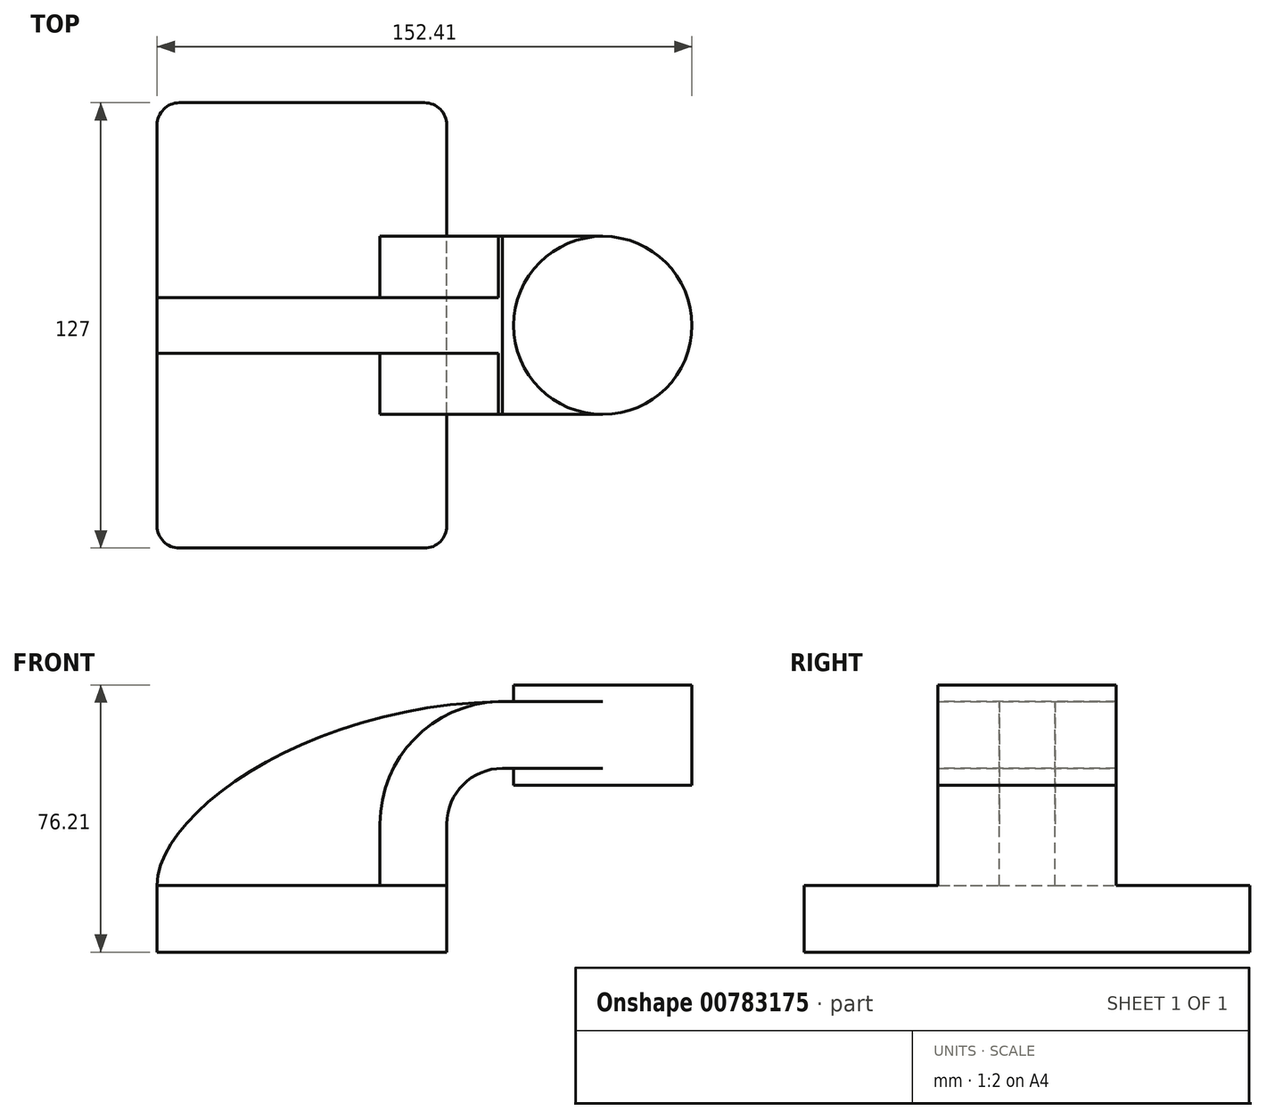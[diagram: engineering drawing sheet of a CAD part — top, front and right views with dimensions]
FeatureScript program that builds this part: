
annotation { "Feature Type Name" : "Feature", "Feature Type Description" : "" }
export const myFeature = defineFeature(function(context is Context, id is Id, definition is map)
    precondition{}
    {
        {
            var Q0;
            Q0=qCreatedBy(makeId("Front.planeOp"),FACE);
            var sketch = newSketch(context, id + "F0", { "sketchPlane" : qUnion([Q0])});
            skLineSegment(sketch, "E0.bottom", {"start": v(41.28, -9.52) * mm, "end": v(-41.28, -9.53) * mm});
            skLineSegment(sketch, "E0.top", {"start": v(41.28, 9.53) * mm, "end": v(-41.28, 9.53) * mm});
            skLineSegment(sketch, "E0.left", {"start": v(41.28, -9.52) * mm, "end": v(41.28, 9.53) * mm});
            skLineSegment(sketch, "E0.right", {"start": v(-41.28, -9.52) * mm, "end": v(-41.28, 9.53) * mm});
            skPoint(sketch, "E0.middle", {"position": v(0, 0) * mm});
            skLineSegment(sketch, "E1.bottom", {"start": v(60.32, 66.68) * mm, "end": v(111.13, 66.68) * mm});
            skLineSegment(sketch, "E1.top", {"start": v(60.32, 38.1) * mm, "end": v(111.13, 38.1) * mm});
            skLineSegment(sketch, "E1.left", {"start": v(60.32, 66.68) * mm, "end": v(60.32, 38.1) * mm});
            skLineSegment(sketch, "E1.right", {"start": v(111.13, 66.68) * mm, "end": v(111.13, 38.1) * mm});
            skPoint(sketch, "E1.middle", {"position": v(85.72, 52.39) * mm});
            skLineSegment(sketch, "E2", {"start": v(41.28, 9.53) * mm, "end": v(41.28, 27) * mm});
            skArc(sketch, "E3", {"start": v(41.27, 27) * mm, "mid": v(45.92, 38.23) * mm, "end": v(57.15, 42.88) * mm});
            skLineSegment(sketch, "E4", {"start": v(57.15, 42.88) * mm, "end": v(85.72, 42.88) * mm});
            skLineSegment(sketch, "E5.0", {"start": v(57.15, 61.93) * mm, "end": v(85.72, 61.93) * mm});
            skArc(sketch, "E5.1", {"start": v(22.23, 27) * mm, "mid": v(32.45, 51.7) * mm, "end": v(57.15, 61.93) * mm});
            skLineSegment(sketch, "E5.2", {"start": v(22.22, 9.53) * mm, "end": v(22.22, 27) * mm});
            skLineSegment(sketch, "E6", {"start": v(85.72, 66.68) * mm, "end": v(85.72, 38.1) * mm});
            skFitSpline(sketch, "E7", {"points": [v(-41.28, 9.52) * mm, v(57.15, 61.93) * mm], "startDerivative": vector(0.87, 64.38) * mm, "endDerivative": vector(161.64, 2.04) * mm});
            skSolve(sketch);
        }
        {
            var Q0;
            Q0=makeQuery(id+"F0.imprint","IMPRINT",FACE,{"disambiguationData":[TD([[makeQuery(id+"F0.imprint","IMPRINT",EDGE,{"derivedFrom":sQuery(id+"F0.wireOp",EDGE,"E0.bottom")}),-1.0]])]});
            extrude(context, id + "F1", {"entities" : qUnion([Q0]), "endBound" : BoundingType.SYMMETRIC, "depth" : 127 * mm, "offsetDistance" : 25.4 * mm});
        }
        {
            var Q0;
            {var subQ1=sQuery(id+"F0.wireOp",EDGE,"E2");Q0=makeQuery(id+"F0.imprint","IMPRINT",FACE,{"disambiguationData":[TD([[makeQuery(id+"F0.imprint","IMPRINT",EDGE,{"derivedFrom":subQ1}),1.0]])]});}
            var Q1;
            {var subQ0=sQuery(id+"F0.wireOp",EDGE,"E5.0");var subQ1=sQuery(id+"F0.wireOp",EDGE,"E1.left");var subQ2=makeQuery(id+"F0.imprint","INTERSECT",VERTEX,{"derivedFrom":[subQ1,subQ0]});Q1=makeQuery(id+"F0.imprint","IMPRINT",FACE,{"disambiguationData":[TD([[makeQuery(id+"F0.imprint","IMPRINT",EDGE,{"disambiguationData":[TD([[subQ2,-1.0]])],"derivedFrom":subQ1}),1.0]])]});}
            extrude(context, id + "F2", {"entities" : qUnion([Q0, Q1]), "operationType" : NewBodyOperationType.ADD, "endBound" : BoundingType.SYMMETRIC, "depth" : 50.8 * mm, "offsetDistance" : 25.4 * mm});
        }
        {
            var Q0;
            {var subQ3=sQuery(id+"F0.wireOp",EDGE,"E5.2");Q0=makeQuery(id+"F0.imprint","IMPRINT",FACE,{"disambiguationData":[TD([[makeQuery(id+"F0.imprint","IMPRINT",EDGE,{"derivedFrom":subQ3}),1.0]])]});}
            extrude(context, id + "F3", {"entities" : qUnion([Q0]), "operationType" : NewBodyOperationType.ADD, "endBound" : BoundingType.SYMMETRIC, "depth" : 15.88 * mm, "offsetDistance" : 25.4 * mm});
        }
        {
            var Q0;
            {var subQ4=sQuery(id+"F0.wireOp",EDGE,"E1.right");Q0=makeQuery(id+"F0.imprint","IMPRINT",FACE,{"disambiguationData":[TD([[makeQuery(id+"F0.imprint","IMPRINT",EDGE,{"derivedFrom":subQ4}),-1.0]])]});}
            var Q1;
            Q1=sQuery(id+"F0.wireOp",EDGE,"E6");
            revolve(context, id + "F4", {"operationType" : NewBodyOperationType.ADD, "surfaceOperationType" : NewSurfaceOperationType.NEW, "entities" : qUnion([Q0]), "axis" : qUnion([Q1]), "revolveType" : RevolveType.FULL});
        }
        {
            var Q0;
            Q0=makeQuery(id+"F1.opExtrude","CAP_EDGE",EDGE,{"disambiguationData":[OSD([sQuery(id+"F0.wireOp",EDGE,"E0.left")])],"isStart":false});
            var Q1;
            Q1=makeQuery(id+"F1.opExtrude","CAP_EDGE",EDGE,{"disambiguationData":[OSD([sQuery(id+"F0.wireOp",EDGE,"E0.right")])],"isStart":false});
            var Q2;
            Q2=makeQuery(id+"F1.opExtrude","CAP_EDGE",EDGE,{"disambiguationData":[OSD([sQuery(id+"F0.wireOp",EDGE,"E0.left")])],"isStart":true});
            var Q3;
            Q3=makeQuery(id+"F1.opExtrude","CAP_EDGE",EDGE,{"disambiguationData":[OSD([sQuery(id+"F0.wireOp",EDGE,"E0.right")])],"isStart":true});
            fillet(context, id + "F5", {"entities" : qUnion([Q0, Q1, Q2, Q3]), "radius" : 6.35 * mm, "tangentPropagation" : true, "allowEdgeOverflow" : false});
        }
    });
